# Revit family: VIESSMANN - Energycal AWH Pro AT 40-65
name_source: partatom
category: Wyposażenie mechaniczne
revit_build: Autodesk Revit 2017 (Build: 20160720_1515(x64)
units: mm (PartAtom-declared; Revit-internal decimal feet)

## family parameters
Numer OmniClass = 23.75.10.21.11
Oparty na płaszczyźnie roboczej = Nie
Punkt obliczania pomieszczeń = Nie
Tnij formami wycięć po wczytaniu = Nie
Typ części = Normalny
Tytuł OmniClass = Air-Source Heat Pumps
Współdzielony = Nie
Wymiar okrągłego złącza = Użyj średnicy
Zawsze pionowo = Tak

## types (4) — shared parameters
Autor = www.archispace.pl
Częstotliwość = 50 Hz
Głębokość = 1208 mm  [stored 3.96325 ft]
Ilość/Obiegi chłodnicze sprężarki (nr/nr) = 1/1
Klasa energetyczna = A+
Liczba biegunów = 3
Liczba wentylatorów = 1
Moc nominalna silnika pompy obiegowej = 1 kW
Moc nominalna wentylatora = 2 kW
Model = Powietrzna pompa ciepła Energycal AWH PRO AT / Air-water heat pump Energycal AWH PRO AT
Napięcie zasilania = 400 V
Nominalna moc pompy = 1 kW
Opis = Energycal AWH Pro AT to typoszereg wysokotemperaturowych pomp ciepła z czynnikiem chłodniczym R134a lub R513A osiągających na zasilaniu temperatury wody do 80°C.
Połączenia hydrauliczne = 1 1/2"
Producent = Viessmann Sp. z o.o
Prąd nominalny wentylatora = 4 A
Stopień wydajności = 2%
Szerokość = 1408 mm  [stored 4.61942 ft]
Typ sprężarki = Reciprocating
Typ wentylatora = Osiowy
Typ wymiennika po stronie grzewczej = Płytowy
URL = https://www.viessmann-projektant.pl
Viessmann Kolor 1 = Viessmann Kolor 2
Viessmann Kolor 2 = Viessmann Kolor 3
Współczynnik mocy = 1
Wysokość = 2390 mm  [stored 7.84121 ft]
Średnica1 = 1 1/2"
Średnica2 = 2"

## per-type parameters (varying)
- Wielkość jednostki - 40: Całkowite napełnienie czynnikiem chłodniczym=18.00 kg; Całkowite napełnienie olejem=4.50 kg; Ciśnienie podnoszenia pompy (A7W45)=185.0 kPa; Efektywność sezonowa ηs=110.8; Maksymalna moc pobierania=21 kW; Maksymalny pobór prądu=49 A; Maksymalny prąd rozruchowy=136 A; Natężenie przepływu wody (A7W45)=1.7 L/s; Natężenie przepływu wody (A7W45) l/h=6268; Nominalna moc grzewcza (A7W45)=37 kW; Obciążenie pozorne=20500 VA; Pobór mocy elektrycznej (A7W45)=11 kW; Poziom ciśnienia akustycznego - wersja cicha LN dB(A)=53 mm  [stored 0.173885 ft]; Poziom ciśnienia akustycznego - wersja super cicha SLN dB(A)=50 mm  [stored 0.164042 ft]; Poziom ciśnienia akustycznego dB(A)=55 mm  [stored 0.180446 ft]; Poziom mocy akustycznej - wersja cicha LN dB(A)=85 mm  [stored 0.278871 ft]; Poziom mocy akustycznej - wersja super cicha SLN dB(A)=83 mm  [stored 0.27231 ft]; Poziom mocy akustycznej dB(A)=87 mm  [stored 0.285433 ft]; Przepływ powietrza=21000.0 m³/h; Prąd nominalny silnika pompy obiegowej=2 A; SCOP=2.84; Spadek ciśnienia wody (A7W45)=19.0 kPa; Współczynnik efektywności [COP] (A7W45)=3.4; Zasilanie elektryczne (V/ph/Hz)=400/N3~/50+5%; Zasilanie opcjonalne (V/ph/Hz)=230/1~/50+5%
- Wielkość jednostki - 45: Całkowite napełnienie czynnikiem chłodniczym=18.00 kg; Całkowite napełnienie olejem=4.50 kg; Ciśnienie podnoszenia pompy (A7W45)=165.0 kPa; Efektywność sezonowa ηs=110.3; Maksymalna moc pobierania=24 kW; Maksymalny pobór prądu=41 A; Maksymalny prąd rozruchowy=151 A; Natężenie przepływu wody (A7W45)=2.0 L/s; Natężenie przepływu wody (A7W45) l/h=7222; Nominalna moc grzewcza (A7W45)=42 kW; Obciążenie pozorne=23800 VA; Pobór mocy elektrycznej (A7W45)=13 kW; Poziom ciśnienia akustycznego - wersja cicha LN dB(A)=53 mm  [stored 0.173885 ft]; Poziom ciśnienia akustycznego - wersja super cicha SLN dB(A)=51 mm; Poziom ciśnienia akustycznego dB(A)=55 mm  [stored 0.180446 ft]; Poziom mocy akustycznej - wersja cicha LN dB(A)=85 mm  [stored 0.278871 ft]; Poziom mocy akustycznej - wersja super cicha SLN dB(A)=83 mm  [stored 0.27231 ft]; Poziom mocy akustycznej dB(A)=87 mm  [stored 0.285433 ft]; Przepływ powietrza=21000.0 m³/h; Prąd nominalny silnika pompy obiegowej=3 A; SCOP=2.83; Spadek ciśnienia wody (A7W45)=21.0 kPa; Współczynnik efektywności [COP] (A7W45)=3.35; Zasilanie elektryczne (V/ph/Hz)=400/3~/50; Zasilanie opcjonalne (V/ph/Hz)=230/1~/50
- Wielkość jednostki - 55: Całkowite napełnienie czynnikiem chłodniczym=25.00 kg; Całkowite napełnienie olejem=4.80 kg; Ciśnienie podnoszenia pompy (A7W45)=115.0 kPa; Efektywność sezonowa ηs=110.5; Maksymalna moc pobierania=30 kW; Maksymalny pobór prądu=64 A; Maksymalny prąd rozruchowy=173 A; Natężenie przepływu wody (A7W45)=2.6 L/s; Natężenie przepływu wody (A7W45) l/h=9313; Nominalna moc grzewcza (A7W45)=54 kW; Obciążenie pozorne=29600 VA; Pobór mocy elektrycznej (A7W45)=16 kW; Poziom ciśnienia akustycznego - wersja cicha LN dB(A)=54 mm  [stored 0.177165 ft]; Poziom ciśnienia akustycznego - wersja super cicha SLN dB(A)=52 mm; Poziom ciśnienia akustycznego dB(A)=56 mm  [stored 0.183727 ft]; Poziom mocy akustycznej - wersja cicha LN dB(A)=86 mm  [stored 0.282152 ft]; Poziom mocy akustycznej - wersja super cicha SLN dB(A)=84 mm  [stored 0.275591 ft]; Poziom mocy akustycznej dB(A)=88 mm  [stored 0.288714 ft]; Przepływ powietrza=20100.0 m³/h; Prąd nominalny silnika pompy obiegowej=2 A; SCOP=2.84; Spadek ciśnienia wody (A7W45)=26.0 kPa; Współczynnik efektywności [COP] (A7W45)=3.4; Zasilanie elektryczne (V/ph/Hz)=400/3N~/50+5%; Zasilanie opcjonalne (V/ph/Hz)=230/1~/50+5%
- Wielkość jednostki - 65: Całkowite napełnienie czynnikiem chłodniczym=29.00 kg; Całkowite napełnienie olejem=4.80 kg; Ciśnienie podnoszenia pompy (A7W45)=153.0 kPa; Efektywność sezonowa ηs=114.8; Maksymalna moc pobierania=63 kW; Maksymalny pobór prądu=19 A; Maksymalny prąd rozruchowy=170 A; Natężenie przepływu wody (A7W45)=3.0 L/s; Natężenie przepływu wody (A7W45) l/h=10832; Nominalna moc grzewcza (A7W45)=63 kW; Obciążenie pozorne=63200 VA; Pobór mocy elektrycznej (A7W45)=19 kW; Poziom ciśnienia akustycznego - wersja cicha LN dB(A)=55 mm  [stored 0.180446 ft]; Poziom ciśnienia akustycznego - wersja super cicha SLN dB(A)=83 mm  [stored 0.27231 ft]; Poziom ciśnienia akustycznego dB(A)=57 mm  [stored 0.187008 ft]; Poziom mocy akustycznej - wersja cicha LN dB(A)=87 mm  [stored 0.285433 ft]; Poziom mocy akustycznej - wersja super cicha SLN dB(A)=85 mm  [stored 0.278871 ft]; Poziom mocy akustycznej dB(A)=89 mm  [stored 0.291995 ft]; Przepływ powietrza=20100.0 m³/h; Prąd nominalny silnika pompy obiegowej=3 A; SCOP=2.95; Spadek ciśnienia wody (A7W45)=27.0 kPa; Współczynnik efektywności [COP] (A7W45)=3.41; Zasilanie elektryczne (V/ph/Hz)=400/3~/50; Zasilanie opcjonalne (V/ph/Hz)=230/1~/50

note: [stored X ft] marks values corroborated as IEEE doubles in the binary element streams (Revit-internal decimal feet)
